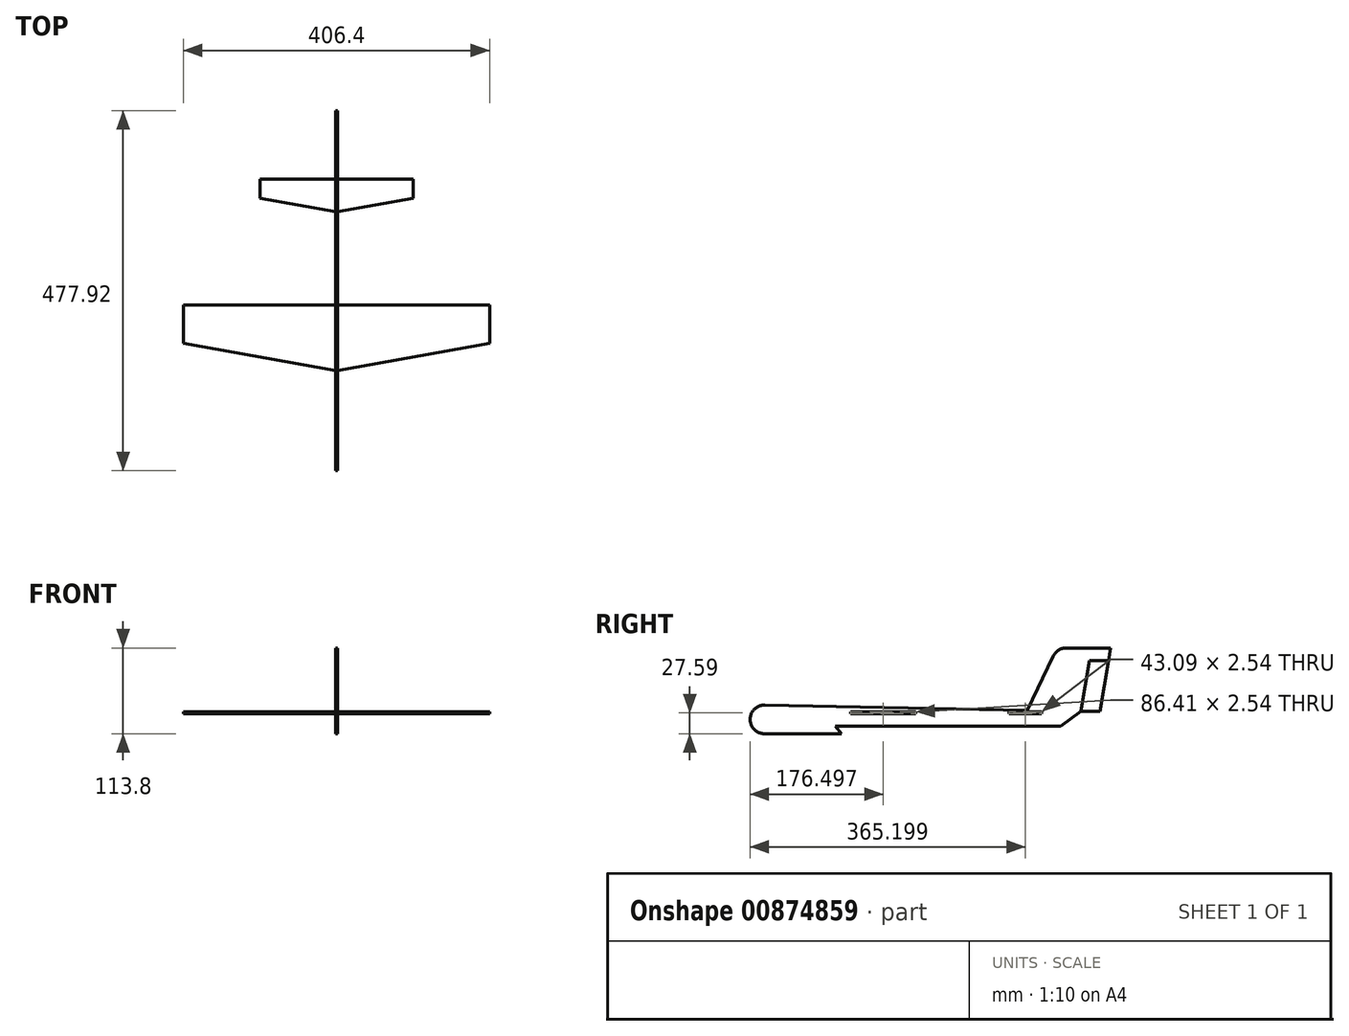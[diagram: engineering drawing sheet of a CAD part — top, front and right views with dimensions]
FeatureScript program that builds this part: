
annotation { "Feature Type Name" : "Feature", "Feature Type Description" : "" }
export const myFeature = defineFeature(function(context is Context, id is Id, definition is map)
    precondition{}
    {
        {
            var Q0;
            Q0=qCreatedBy(makeId("Right.planeOp"),FACE);
            var sketch = newSketch(context, id + "F0", { "sketchPlane" : qUnion([Q0])});
            skCircle(sketch, "E0", {"center": v(-200.65, -7.27) * mm, "radius": 19.05 * mm});
            skLineSegment(sketch, "E1", {"start": v(-200.27, -26.31) * mm, "end": v(-98.67, -26.31) * mm});
            skLineSegment(sketch, "E2", {"start": v(-98.67, -26.31) * mm, "end": v(-106.73, -16.5) * mm});
            skLineSegment(sketch, "E3", {"start": v(-200.26, 11.78) * mm, "end": v(148.11, 4.56) * mm});
            skLineSegment(sketch, "E4", {"start": v(-106.73, -16.5) * mm, "end": v(192.1, -16.5) * mm});
            skLineSegment(sketch, "E5", {"start": v(244.7, 3.58) * mm, "end": v(258.22, 87.48) * mm});
            skLineSegment(sketch, "E6", {"start": v(258.22, 87.48) * mm, "end": v(199.87, 87.48) * mm});
            skArc(sketch, "E7", {"start": v(199.87, 87.48) * mm, "mid": v(189.56, 84.5) * mm, "end": v(182.43, 76.47) * mm});
            skLineSegment(sketch, "E8", {"start": v(182.43, 76.47) * mm, "end": v(148.11, 4.56) * mm});
            skLineSegment(sketch, "E9", {"start": v(244.7, 3.58) * mm, "end": v(219.3, 3.58) * mm});
            skLineSegment(sketch, "E10", {"start": v(219.3, 3.58) * mm, "end": v(192.1, -16.5) * mm});
            skLineSegment(sketch, "E11", {"start": v(255.56, 70.95) * mm, "end": v(230.16, 70.95) * mm});
            skLineSegment(sketch, "E12", {"start": v(230.16, 70.95) * mm, "end": v(219.3, 3.58) * mm});
            skSolve(sketch);
        }
        {
            var Q0;
            {var subQ1=sQuery(id+"F0.wireOp",EDGE,"E1");Q0=makeQuery(id+"F0.imprint","IMPRINT",FACE,{"disambiguationData":[TD([[makeQuery(id+"F0.imprint","IMPRINT",EDGE,{"derivedFrom":subQ1}),1.0]])]});}
            var Q1;
            {var subQ0=sQuery(id+"F0.wireOp",EDGE,"E0");var subQ1=makeQuery(id+"F0.imprint","INTERSECT",VERTEX,{"derivedFrom":[subQ0,sQuery(id+"F0.wireOp",EDGE,"E1")]});Q1=makeQuery(id+"F0.imprint","IMPRINT",FACE,{"disambiguationData":[TD([[makeQuery(id+"F0.imprint","IMPRINT",EDGE,{"disambiguationData":[TD([[subQ1,1.0]])],"derivedFrom":subQ0}),1.0]])]});}
            extrude(context, id + "F1", {"entities" : qUnion([Q0, Q1]), "depth" : 1.27 * mm, "offsetDistance" : 25.4 * mm});
        }
        {
            var Q0;
            Q0=makeQuery(id+"F1.opExtrude","SWEPT_BODY",BODY,{"disambiguationData":[OSD([sQuery(id+"F0.wireOp",EDGE,"E0"),sQuery(id+"F0.wireOp",EDGE,"E1"),sQuery(id+"F0.wireOp",EDGE,"E2"),sQuery(id+"F0.wireOp",EDGE,"E3"),sQuery(id+"F0.wireOp",EDGE,"E4"),sQuery(id+"F0.wireOp",EDGE,"E5"),sQuery(id+"F0.wireOp",EDGE,"E6"),sQuery(id+"F0.wireOp",EDGE,"E7"),sQuery(id+"F0.wireOp",EDGE,"E8"),sQuery(id+"F0.wireOp",EDGE,"4MPfE3jW-YjWQ-WMdw-mN1b-GvhTEKniSUGy")])]});
            var Q1;
            Q1=qCreatedBy(makeId("Right.planeOp"),FACE);
            mirror(context, id + "F2", {"operationType" : NewBodyOperationType.ADD, "entities" : qUnion([Q0]), "mirrorPlane" : qUnion([Q1])});
        }
        {
            var Q0;
            {var subQ0=sQuery(id+"F0.wireOp",EDGE,"E9");Q0=makeQuery(id+"F0.imprint","IMPRINT",FACE,{"disambiguationData":[TD([[makeQuery(id+"F0.imprint","IMPRINT",EDGE,{"derivedFrom":subQ0}),-1.0]])]});}
            extrude(context, id + "F3", {"entities" : qUnion([Q0]), "depth" : 0.64 * mm, "offsetDistance" : 25.4 * mm});
        }
        {
            var Q0;
            Q0=makeQuery(id+"F3.opExtrude","SWEPT_BODY",BODY,{"disambiguationData":[OSD([sQuery(id+"F0.wireOp",EDGE,"E5"),sQuery(id+"F0.wireOp",EDGE,"E9"),sQuery(id+"F0.wireOp",EDGE,"E11"),sQuery(id+"F0.wireOp",EDGE,"E12")])]});
            var Q1;
            Q1=qCreatedBy(makeId("Right.planeOp"),FACE);
            mirror(context, id + "F4", {"entities" : qUnion([Q0]), "mirrorPlane" : qUnion([Q1])});
        }
        {
            var Q0;
            Q0=qCreatedBy(makeId("Top.planeOp"),FACE);
            var sketch = newSketch(context, id + "F5", { "sketchPlane" : qUnion([Q0])});
            skLineSegment(sketch, "E13", {"start": v(0, 0) * mm, "end": v(-203.2, 0) * mm});
            skLineSegment(sketch, "E14", {"start": v(-203.2, 0) * mm, "end": v(-203.2, -50.8) * mm});
            skLineSegment(sketch, "E15", {"start": v(-203.2, -50.8) * mm, "end": v(0, -86.63) * mm});
            skLineSegment(sketch, "E16.MirrorCS", {"start": v(0, 0) * mm, "end": v(203.2, 0) * mm});
            skLineSegment(sketch, "E17.MirrorCS", {"start": v(203.2, 0) * mm, "end": v(203.2, -50.8) * mm});
            skLineSegment(sketch, "E18.MirrorCS", {"start": v(203.2, -50.8) * mm, "end": v(0, -86.63) * mm});
            skSolve(sketch);
        }
        {
            var Q0;
            Q0=makeQuery(id+"F5.imprint","IMPRINT",FACE,{"disambiguationData":[TD([[makeQuery(id+"F5.imprint","IMPRINT",EDGE,{"derivedFrom":sQuery(id+"F5.wireOp",EDGE,"E13")}),1.0]])]});
            extrude(context, id + "F6", {"entities" : qUnion([Q0]), "operationType" : NewBodyOperationType.ADD, "depth" : 2.54 * mm, "offsetDistance" : 25.4 * mm});
        }
        {
            var Q0;
            Q0=qCreatedBy(makeId("Top.planeOp"),FACE);
            var sketch = newSketch(context, id + "F7", { "sketchPlane" : qUnion([Q0])});
            skLineSegment(sketch, "E19", {"start": v(0, 167.04) * mm, "end": v(-101.6, 167.04) * mm});
            skLineSegment(sketch, "E20", {"start": v(-101.6, 167.04) * mm, "end": v(-101.6, 141.64) * mm});
            skLineSegment(sketch, "E21", {"start": v(-101.6, 141.64) * mm, "end": v(0, 123.73) * mm});
            skLineSegment(sketch, "E22.MirrorCS", {"start": v(0, 167.04) * mm, "end": v(101.6, 167.04) * mm});
            skLineSegment(sketch, "E23.MirrorCS", {"start": v(101.6, 141.64) * mm, "end": v(0, 123.73) * mm});
            skLineSegment(sketch, "E24.MirrorCS", {"start": v(101.6, 167.04) * mm, "end": v(101.6, 141.64) * mm});
            skSolve(sketch);
        }
        {
            var Q0;
            Q0=makeQuery(id+"F7.imprint","IMPRINT",FACE,{"disambiguationData":[TD([[makeQuery(id+"F7.imprint","IMPRINT",EDGE,{"derivedFrom":sQuery(id+"F7.wireOp",EDGE,"E19")}),1.0]])]});
            extrude(context, id + "F8", {"entities" : qUnion([Q0]), "operationType" : NewBodyOperationType.ADD, "depth" : 2.54 * mm, "offsetDistance" : 25.4 * mm});
        }
    });
